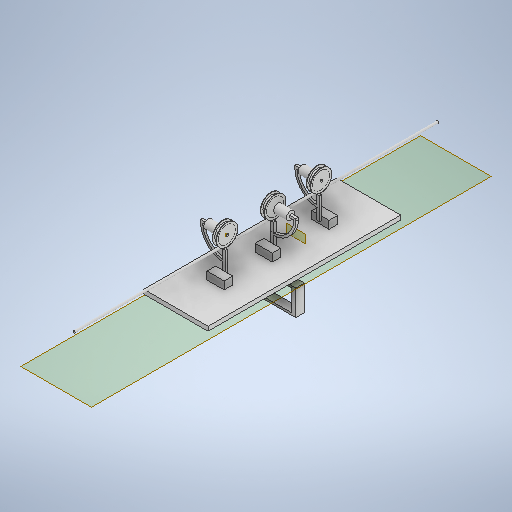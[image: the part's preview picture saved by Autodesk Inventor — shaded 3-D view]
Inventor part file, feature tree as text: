
AUTODESK INVENTOR PART (.ipt)
format: ipt  version: 2025 (Build 290162000, 162)  size: 545,792 bytes
history: native  units: mm
features: sketch x24, extrude x22, plane x6, mirror x6
ambient origin geometry x8: Origin, YZ Plane, XZ Plane, XY Plane, X Axis, Y Axis, Z Axis, Center Point
bodies: Solid1 (feature_tree)
feature tree (58):
  extrude  "Extrusion1"  Depth=450.0mm
  extrude  "Extrusion2"  Depth=10.0mm TaperAngle=0.0deg
  extrude  "Extrusion3"  Depth=30.0mm TaperAngle=0.0deg
  extrude  "Extrusion4"  [1 undecoded]
  extrude  "Extrusion5"  [1 undecoded]
  plane  "Work Plane1"
  sketch  "Sketch6"  dims[d27=50.0mm d28=-4.0mm]
  plane  "Work Plane2"
  sketch  "Sketch7"  dims[d29=50.0mm d30=1.0mm d31=0.0mm]
  plane  "Work Plane3"
  sketch  "Sketch8"  dims[d32=1.0mm d33=0.0mm d34=8.5mm d35=0.0mm]
  extrude  "Extrusion6"  [1 undecoded]
  extrude  "Extrusion7"  Depth=1.0mm TaperAngle=0.0deg
  extrude  "Extrusion8"  Depth=1.0mm TaperAngle=0.0deg
  mirror  "Mirror1"
  mirror  "Mirror2"
  mirror  "Mirror3"
  mirror  "Mirror4"
  sketch  "Sketch9"  dims[d36=6.0mm d37=0.0mm d38=20.0mm]
  sketch  "Sketch10"  dims[d39=30.0mm d40=0.0mm d41=56.25mm]
  sketch  "Sketch11"  dims[d42=30.0mm d43=0.0mm d44=30.0mm d45=0.0mm]
  extrude  "Extrusion9"  Depth=20.0mm
  extrude  "Extrusion10"  Depth=30.0mm
  plane  "Work Plane4"
  mirror  "Mirror5"
  mirror  "Mirror6"
  extrude  "Extrusion11"  Depth=30.0mm TaperAngle=0.0deg
  extrude  "Extrusion12"  Depth=75.0mm
  extrude  "Extrusion13"  Depth=6.0mm
  extrude  "Extrusion14"  Depth=20.0mm
  extrude  "Extrusion15"  Depth=7.0mm TaperAngle=0.0deg
  extrude  "Extrusion16"  Depth=7.0mm
  plane  "Work Plane6"
  extrude  "Extrusion17"  Depth=15.0mm TaperAngle=0.0deg
  extrude  "Extrusion18"  Depth=20.0mm
  extrude  "Extrusion19"  Depth=10.0mm
  extrude  "Extrusion20"  Depth=50.0mm TaperAngle=0.0deg
  extrude  "Extrusion21"  Depth=7.0mm
  extrude  "Extrusion22"  Depth=25.0mm
  sketch  "Sketch1"  dims[d0=150.0mm d1=450.0mm]
  sketch  "Sketch2"  dims[d2=10.0mm d3=0.0mm d9=18.0mm d10=0.0mm]
  sketch  "Sketch3"  dims[d17=5.0mm d18=0.0mm d20=30.0mm d21=0.0mm]
  sketch  "Sketch4"  dims[d22=16.0mm d23=0.0mm d24=-6.5mm]
  sketch  "Sketch5"  dims[d25=40.0mm d26=-2.5mm]
  sketch  "Sketch12"  dims[d48=350.0mm d49=499.0mm d50=0.0mm d51=0.0mm d52=75.0mm]
  plane  "Work Plane5"
  sketch  "Sketch13"  dims[d53=250.0mm d54=6.0mm]
  sketch  "Sketch14"  dims[d55=20.0mm d56=0.0mm d57=200.0mm]
  sketch  "Sketch15"  dims[d58=7.0mm d59=300.0mm d60=0.0mm]
  sketch  "Sketch16"  dims[d61=10.0mm d62=85.0mm d63=0.0mm d64=0.0mm d65=7.0mm]
  sketch  "Sketch17"  dims[d66=7.0mm d67=15.0mm d68=3.5mm d69=0.0mm d70=0.0mm]
  sketch  "Sketch18"  dims[d71=130.0mm d72=20.0mm]
  sketch  "Sketch19"  dims[d73=5.0mm d74=0.0mm d75=10.0mm]
  sketch  "Sketch20"  dims[d76=10.0mm d77=50.0mm d78=0.0mm]
  sketch  "Sketch21"  dims[d79=5.0mm d80=0.0mm d82=7.0mm]
  sketch  "Sketch22"  dims[d83=10.0mm d84=20.0mm d85=0.0mm d86=0.0mm d87=25.0mm]
  sketch  "Sketch23"  dims[d88=20.0mm]
  sketch  "Sketch24"  dims[d89=30.0mm d90=0.0mm]
note: 3 required parameter values undecoded (feature->parameter linkage not recoverable at this tier; creation-order binding heuristic only, values carry confidence <= 0.55)
